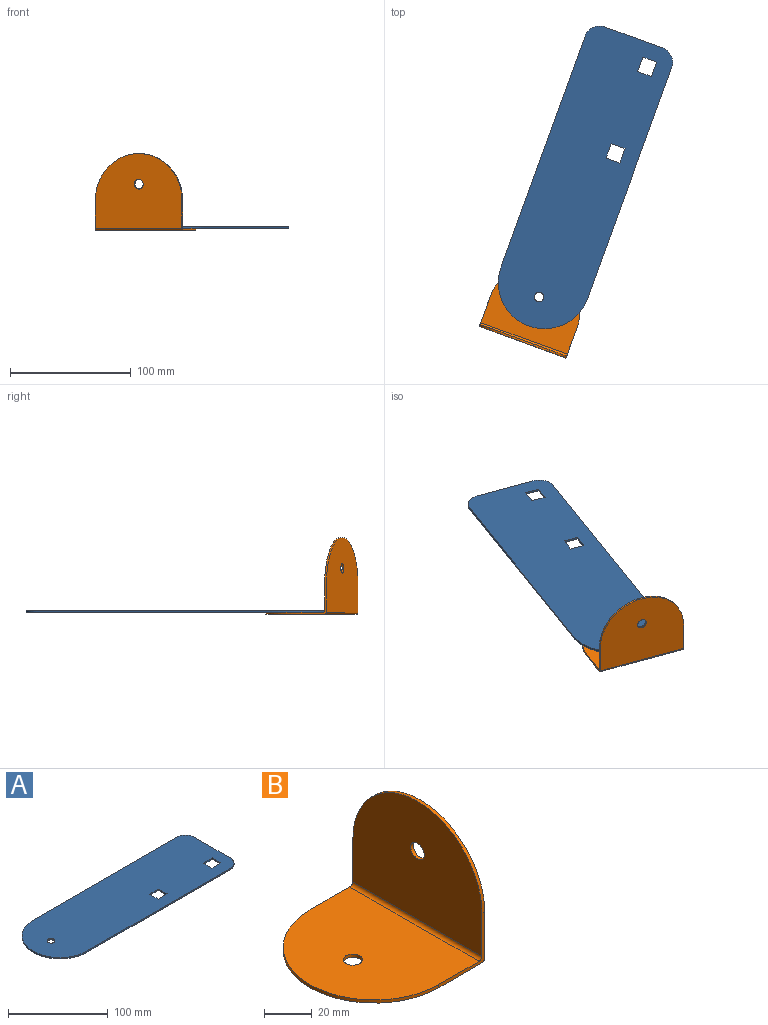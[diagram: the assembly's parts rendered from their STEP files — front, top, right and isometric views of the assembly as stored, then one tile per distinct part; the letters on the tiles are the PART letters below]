
ASSEMBLY  parts=2 mates=1
PART A: 17 faces, bbox 254x76.2x1.6 mm
  f0: plane 12.7x1.6mm, normal (0,-1,0), area 20.3mm2, adj f1,f14,f15,f16
  f1: plane 12.07x1.6mm, normal (-1,0,0), area 19.3mm2, adj f0,f2,f15,f16
  f2: plane 12.7x1.6mm, normal (0,1,0), area 20.3mm2, adj f1,f14,f15,f16
  f3: plane 203.2x1.6mm, normal (0,1,0), area 325.2mm2, adj f4,f12,f15,f16
  f4: cylinder r=38.1mm len=76.2mm, axis (0,0,-1), area 191.5mm2, adj f3,f5,f15,f16
  f5: plane 203.2x1.6mm, normal (0,-1,0), area 325.2mm2, adj f4,f6,f15,f16
  f6: cylinder r=12.7mm len=12.7mm, axis (0,0,-1), area 31.9mm2, adj f5,f7,f15,f16
  f7: plane 50.8x1.6mm, normal (1,0,0), area 81.3mm2, adj f6,f12,f15,f16
  f8: plane 12.07x1.6mm, normal (1,0,0), area 19.3mm2, adj f9,f13,f15,f16
  f9: plane 12.7x1.6mm, normal (0,-1,0), area 20.3mm2, adj f8,f10,f15,f16
  f10: plane 12.07x1.6mm, normal (-1,0,0), area 19.3mm2, adj f9,f13,f15,f16
  f11: cylinder r=3.97mm len=7.94mm, axis (0,0,-1), area 39.9mm2, adj f15,f16
  f12: cylinder r=12.7mm len=12.7mm, axis (0,0,-1), area 31.9mm2, adj f3,f7,f15,f16
  f13: plane 12.7x1.6mm, normal (0,1,0), area 20.3mm2, adj f8,f10,f15,f16
  f14: plane 12.07x1.6mm, normal (1,0,0), area 19.3mm2, adj f0,f2,f15,f16
  f15: plane 254x76.2mm, normal (0,0,1), area 18306.6mm2, adj f0,f1,f2,f3,f4,f5,f6,f7
  f16: plane 254x76.2mm, normal (0,0,-1), area 18306.6mm2, adj f0,f1,f2,f3,f4,f5,f6,f7
PART B: 12 faces, bbox 65.1x76.2x63.5 mm
  f0: plane 27x25.4mm, normal (0,1,0), area 81.3mm2, adj f1,f4,f5,f6,f7,f9,f10,f11
  f1: cylinder r=38.1mm len=76.2mm, axis (0,0,-1), area 191.5mm2, adj f0,f3,f4,f5
  f2: cylinder r=3.97mm len=7.94mm, axis (0,0,-1), area 39.9mm2, adj f4,f5
  f3: plane 27x25.4mm, normal (0,-1,0), area 81.3mm2, adj f1,f4,f5,f6,f7,f9,f10,f11
  f4: plane 76.2x61.75mm, normal (0,0,1), area 4032.6mm2, adj f0,f1,f2,f3,f11
  f5: plane 76.2x63.35mm, normal (0,0,-1), area 4154.6mm2, adj f0,f1,f2,f3,f10
  f6: plane 76.2x60.15mm, normal (-1,0,0), area 3910.7mm2, adj f0,f3,f7,f8,f11
  f7: cylinder r=38.1mm len=76.2mm, axis (-1,0,0), area 191.5mm2, adj f0,f3,f6,f9
  f8: cylinder r=3.97mm len=7.94mm, axis (-1,0,0), area 39.9mm2, adj f6,f9
  f9: plane 76.2x61.75mm, normal (1,0,0), area 4032.6mm2, adj f0,f3,f7,f8,f10
  f10: cylinder r=1.75mm len=76.2mm, axis (0,1,0), area 209.8mm2, adj f0,f3,f5,f9
  f11: cylinder r=1.75mm len=76.2mm, axis (0,-1,0), area 209.8mm2, adj f0,f3,f4,f6
PLACE A rot(axis=(0,0,1),70deg) t=(-56.68,86.31,-22.47)mm
PLACE B rot(axis=(0,0,-1),110deg) t=(-104.47,-44.97,-24.07)mm
MATE revolute B.f2 <-> A.f11  axis (0,0,-1) through (-91.43,-9.16,-24.07)mm
